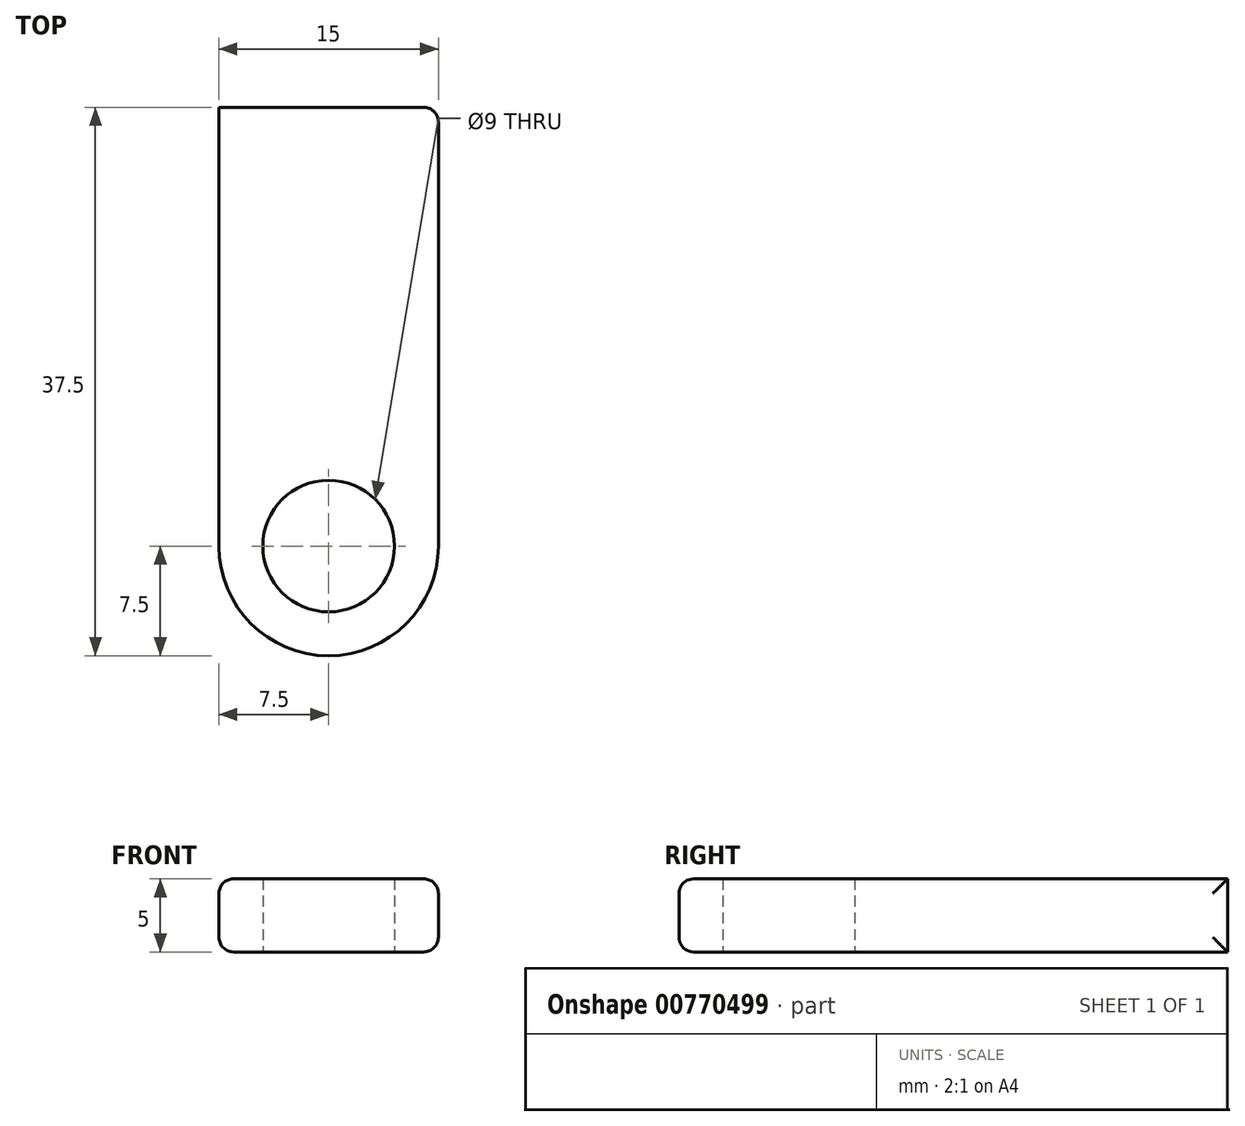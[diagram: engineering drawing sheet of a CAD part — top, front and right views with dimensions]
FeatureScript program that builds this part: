
annotation { "Feature Type Name" : "Feature", "Feature Type Description" : "" }
export const myFeature = defineFeature(function(context is Context, id is Id, definition is map)
    precondition{}
    {
        {
            var Q0;
            Q0=qCreatedBy(makeId("Top.planeOp"),FACE);
            var sketch = newSketch(context, id + "F0", { "sketchPlane" : qUnion([Q0])});
            skLineSegment(sketch, "E0.top", {"start": v(-7.5, 11.2) * mm, "end": v(7.5, 11.2) * mm});
            skLineSegment(sketch, "E0.left", {"start": v(-7.5, -18.8) * mm, "end": v(-7.5, 11.2) * mm});
            skLineSegment(sketch, "E0.right", {"start": v(7.5, -18.8) * mm, "end": v(7.5, 11.2) * mm});
            skArc(sketch, "E1", {"start": v(-7.5, -18.8) * mm, "mid": v(0, -26.3) * mm, "end": v(7.5, -18.8) * mm});
            skCircle(sketch, "E2", {"center": v(0, -18.8) * mm, "radius": 4.5 * mm});
            skSolve(sketch);
        }
        {
            var Q0;
            Q0=makeQuery(id+"F0.imprint","IMPRINT",FACE,{"disambiguationData":[TD([[makeQuery(id+"F0.imprint","IMPRINT",EDGE,{"derivedFrom":sQuery(id+"F0.wireOp",EDGE,"E0.top")}),-1.0]])]});
            extrude(context, id + "F1", {"entities" : qUnion([Q0]), "depth" : 5 * mm, "offsetDistance" : 25 * mm});
        }
        {
            var Q0;
            Q0=makeQuery(id+"F1.opExtrude","SWEPT_FACE",FACE,{"disambiguationData":[OSD([sQuery(id+"F0.wireOp",EDGE,"E0.right")])]});
            fillet(context, id + "F2", {"entities" : qUnion([Q0]), "radius" : 1 * mm, "tangentPropagation" : true, "allowEdgeOverflow" : false});
        }
    });
